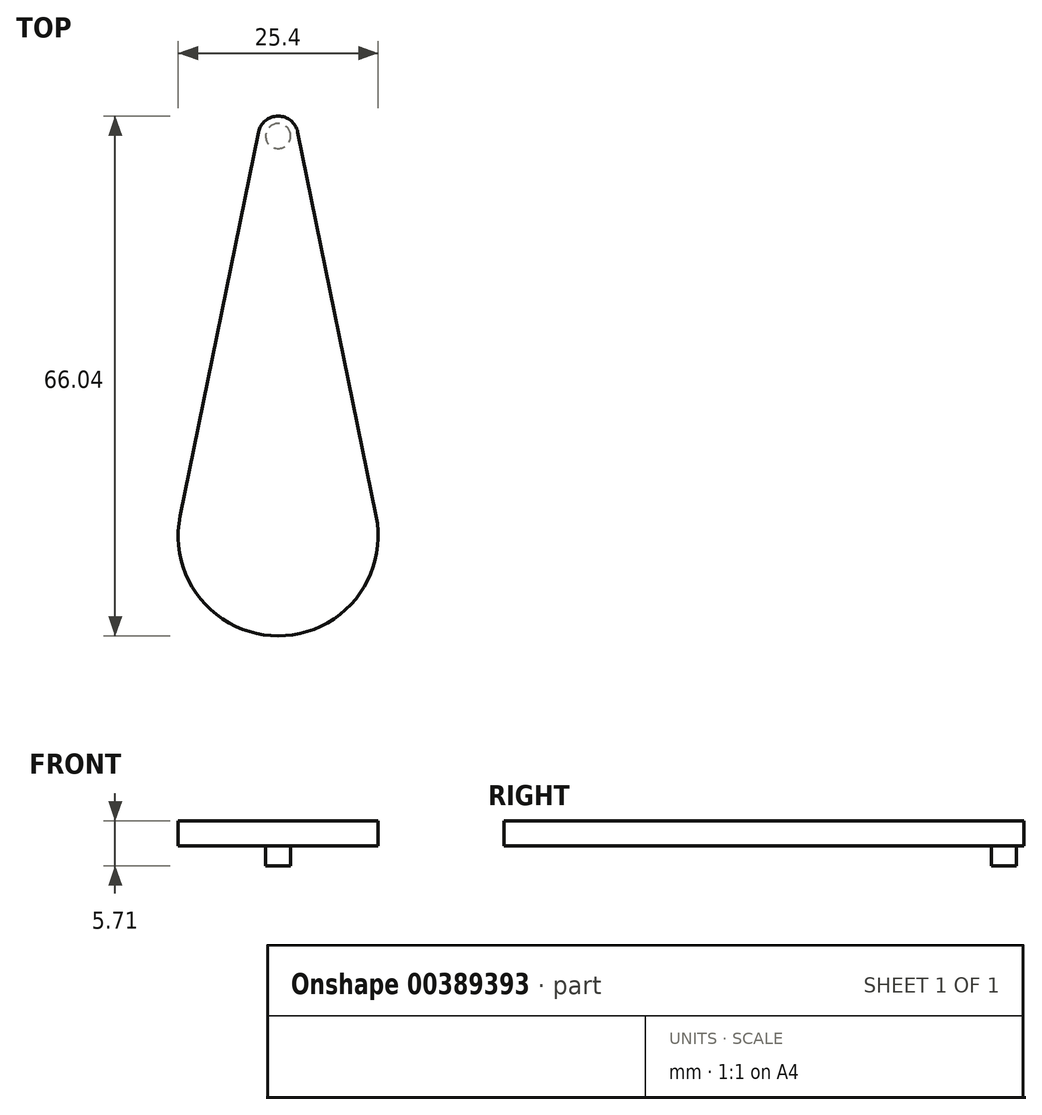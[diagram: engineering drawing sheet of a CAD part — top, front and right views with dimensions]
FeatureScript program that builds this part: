
annotation { "Feature Type Name" : "Feature", "Feature Type Description" : "" }
export const myFeature = defineFeature(function(context is Context, id is Id, definition is map)
    precondition{}
    {
        {
            var Q0;
            Q0=qCreatedBy(makeId("Top.planeOp"),FACE);
            var sketch = newSketch(context, id + "F0", { "sketchPlane" : qUnion([Q0])});
            skArc(sketch, "E0", {"start": v(2.49, 0.5) * mm, "mid": v(0, 2.54) * mm, "end": v(-2.49, 0.5) * mm});
            skArc(sketch, "E1", {"start": v(-12.44, -48.26) * mm, "mid": v(0, -63.5) * mm, "end": v(12.44, -48.26) * mm});
            skLineSegment(sketch, "E2", {"start": v(-2.49, 0.5) * mm, "end": v(-12.44, -48.26) * mm});
            skLineSegment(sketch, "E3", {"start": v(2.49, 0.5) * mm, "end": v(12.44, -48.26) * mm});
            skCircle(sketch, "E4", {"center": v(0, 0) * mm, "radius": 1.59 * mm});
            skSolve(sketch);
        }
        {
            var Q0;
            Q0 = qSketchRegion(id + "F0", true);
            var Q1;
            Q1=makeQuery(id+"F0.imprint","IMPRINT",FACE,{"disambiguationData":[TD([[makeQuery(id+"F0.imprint","IMPRINT",EDGE,{"derivedFrom":sQuery(id+"F0.wireOp",EDGE,"E4")}),1.0]])]});
            extrude(context, id + "F1", {"entities" : qUnion([Q0, Q1]), "depth" : 3.17 * mm});
        }
        {
            var Q0;
            Q0=makeQuery(id+"F0.imprint","IMPRINT",FACE,{"disambiguationData":[TD([[makeQuery(id+"F0.imprint","IMPRINT",EDGE,{"derivedFrom":sQuery(id+"F0.wireOp",EDGE,"E4")}),1.0]])]});
            extrude(context, id + "F2", {"entities" : qUnion([Q0]), "operationType" : NewBodyOperationType.ADD, "oppositeDirection" : true, "depth" : 2.54 * mm});
        }
    });
